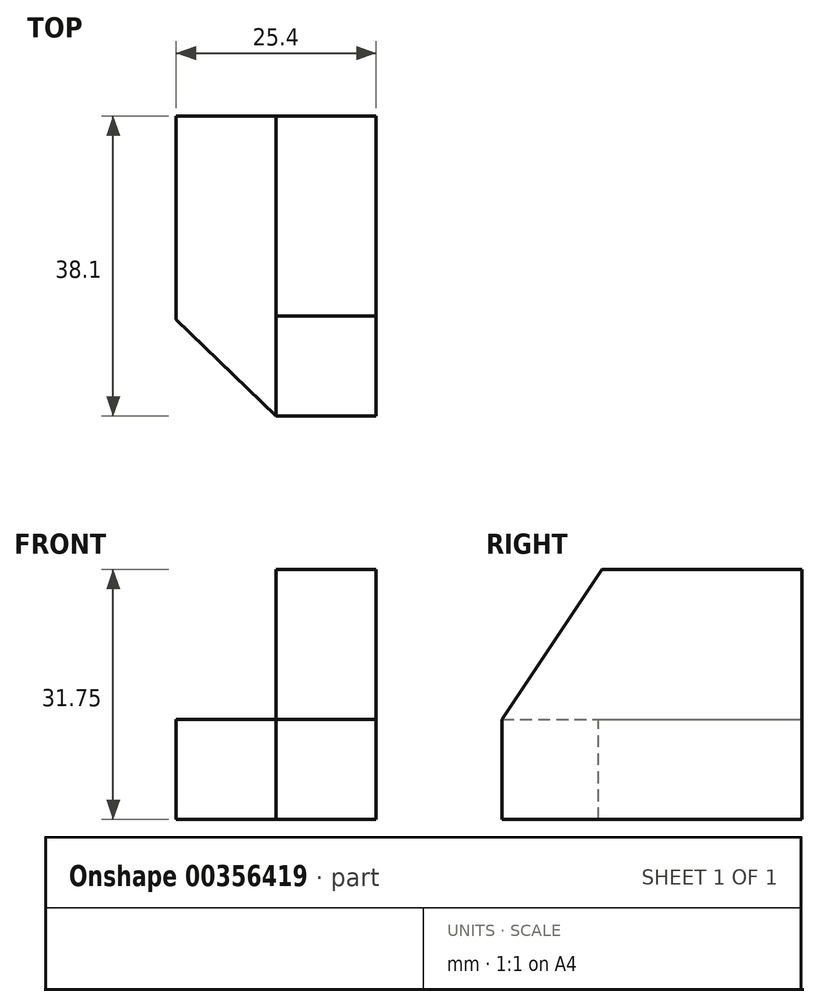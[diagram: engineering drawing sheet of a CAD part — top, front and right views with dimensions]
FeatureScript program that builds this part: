
annotation { "Feature Type Name" : "Feature", "Feature Type Description" : "" }
export const myFeature = defineFeature(function(context is Context, id is Id, definition is map)
    precondition{}
    {
        {
            var Q0;
            Q0=qCreatedBy(makeId("Front.planeOp"),FACE);
            var sketch = newSketch(context, id + "F0", { "sketchPlane" : qUnion([Q0])});
            skLineSegment(sketch, "E0", {"start": v(0, 12.7) * mm, "end": v(0, 0) * mm});
            skLineSegment(sketch, "E1", {"start": v(0, 0) * mm, "end": v(12.7, 0) * mm});
            skLineSegment(sketch, "E2", {"start": v(12.7, 0) * mm, "end": v(12.7, 12.7) * mm});
            skLineSegment(sketch, "E3", {"start": v(12.7, 12.7) * mm, "end": v(0, 12.7) * mm});
            skSolve(sketch);
        }
        {
            var Q0;
            Q0 = qSketchRegion(id + "F0", true);
            extrude(context, id + "F1", {"entities" : qUnion([Q0]), "depth" : 38.1 * mm});
        }
        {
            var Q0;
            Q0=makeQuery(id+"F1.opExtrude","SWEPT_FACE",FACE,{"disambiguationData":[OSD([sQuery(id+"F0.wireOp",EDGE,"E0")])]});
            var sketch = newSketch(context, id + "F2", { "sketchPlane" : qUnion([Q0])});
            skLineSegment(sketch, "E4", {"start": v(38.1, 12.7) * mm, "end": v(25.4, 31.75) * mm});
            skLineSegment(sketch, "E5", {"start": v(25.4, 31.75) * mm, "end": v(0, 31.75) * mm});
            skLineSegment(sketch, "E6", {"start": v(0, 31.75) * mm, "end": v(0, 12.7) * mm});
            skLineSegment(sketch, "E7", {"start": v(0, 12.7) * mm, "end": v(38.1, 12.7) * mm});
            skSolve(sketch);
        }
        {
            var Q0;
            Q0 = qSketchRegion(id + "F2", true);
            extrude(context, id + "F3", {"entities" : qUnion([Q0]), "operationType" : NewBodyOperationType.ADD, "oppositeDirection" : true, "depth" : 12.7 * mm});
        }
        {
            var Q0;
            Q0=qCreatedBy(makeId("Front.planeOp"),FACE);
            var sketch = newSketch(context, id + "F4", { "sketchPlane" : qUnion([Q0])});
            skLineSegment(sketch, "E8", {"start": v(0, 12.7) * mm, "end": v(-12.7, 12.7) * mm});
            skLineSegment(sketch, "E9", {"start": v(-12.7, 12.7) * mm, "end": v(-12.7, 0) * mm});
            skLineSegment(sketch, "E10", {"start": v(-12.7, 0) * mm, "end": v(0, 0) * mm});
            skLineSegment(sketch, "E11", {"start": v(0, 0) * mm, "end": v(0, 12.7) * mm});
            skSolve(sketch);
        }
        {
            var Q0;
            Q0 = qSketchRegion(id + "F4", true);
            extrude(context, id + "F5", {"entities" : qUnion([Q0]), "operationType" : NewBodyOperationType.ADD, "depth" : 38.1 * mm});
        }
        {
            var Q0;
            Q0=makeQuery(id+"F5.opExtrude","SWEPT_FACE",FACE,{"disambiguationData":[OSD([sQuery(id+"F4.wireOp",EDGE,"E8")])]});
            var sketch = newSketch(context, id + "F6", { "sketchPlane" : qUnion([Q0])});
            skLineSegment(sketch, "E12", {"start": v(0, -38.1) * mm, "end": v(-12.7, -25.84) * mm});
            skSolve(sketch);
        }
        {
            var Q0;
            Q0 = qSketchRegion(id + "F6", true);
            var Q1;
            {var subQ0=sQuery(id+"F6.wireOp",EDGE,"E12");Q1=makeQuery(id+"F6.imprint","IMPRINT",FACE,{"disambiguationData":[TD([[makeQuery(id+"F6.imprint","IMPRINT",EDGE,{"derivedFrom":subQ0}),1.0]])]});}
            extrude(context, id + "F7", {"entities" : qUnion([Q0, Q1]), "operationType" : NewBodyOperationType.REMOVE, "oppositeDirection" : true, "depth" : 25.4 * mm});
        }
    });
